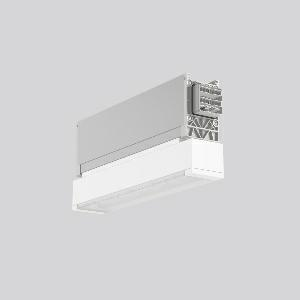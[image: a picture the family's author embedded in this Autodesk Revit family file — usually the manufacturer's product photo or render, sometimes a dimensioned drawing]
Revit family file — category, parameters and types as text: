
# Revit family: linedo_module_rt_9503rt_760_430_0hc_dd67
name_source: partatom
category: Lighting Fixtures
units: mm (PartAtom-declared; Revit-internal decimal feet)

## family parameters
Cut with Voids When Loaded = No
Host = Face
Light Source = No
Part Type = Normal
Room Calculation Point = No
Round Connector Dimension = Use Diameter
Shared = No

## types (1)
- LINEDO Module RT (1 x LED Modul 763, 480 lm, 6300)
    Apparent Load = 6 VA
    CIE Flux Codes = 85 95 99 99 100
    Color Rendering = 70
    Color Temperature = 6300
    Default Elevation = 1800 mm
    Description = LINEDO, 6 W, 480 lm, 763, aluminium, on/off
Continuous line luminaire, L 342 B 58 H 147, SBS, 3 h, emergency-220 lm, automatischer Selbsttest
Project solution!
    Height = 147 mm
    Lamp = 1 x LED Modul 763
    Lamp Light Flux = 480 lm
    Lamp count = 1
    Length = 342 mm
    Lifetime = 50000 h
    Luminous efficacy = 80 lm/W
    Manufacturer = RZB
    ModVariant = No
    Model = 9503RT.760.430.0HC
    Mounting Place = Ceiling
    Mounting Type = Surface mounted
    Number of Poles = 1
    OnlyDefault = Yes
    Power Factor = 1
    Product Name = LINEDO Module RT
    Product group = Continuous line luminaire system Linedo IP 54
    ProductGroupID = 314
    Protection Class = Protection class I
    Protection Degree = IP 54
    RLX_Detail_Level = 1
    RLX_Emergency_Light_Flux = 220 lm
    RLX_Emergency_Type = 3
    RLX_Emergency_Type_DB = Yes
    RlxData = <blob elided: 19909 chars, md5=5f8563c4>
    Socket = socket
    Standby Power = 0 W
    System Light Flux = 480 lm
    System Power = 6 W
    Type Comments = Product without accessories
    Type Image = 9503rf.760.430.0hc.jpg
    URL = http://relux.com
    VarID = ---
    Voltage = 230 V
    Voltage Range = 220-240 V
    Weight = 0.00 kg
    Width = 58 mm

## geometry (parser evidence)
native form markers: Blend x4, Sweep x11
no freeform markers — native parametric forms only
